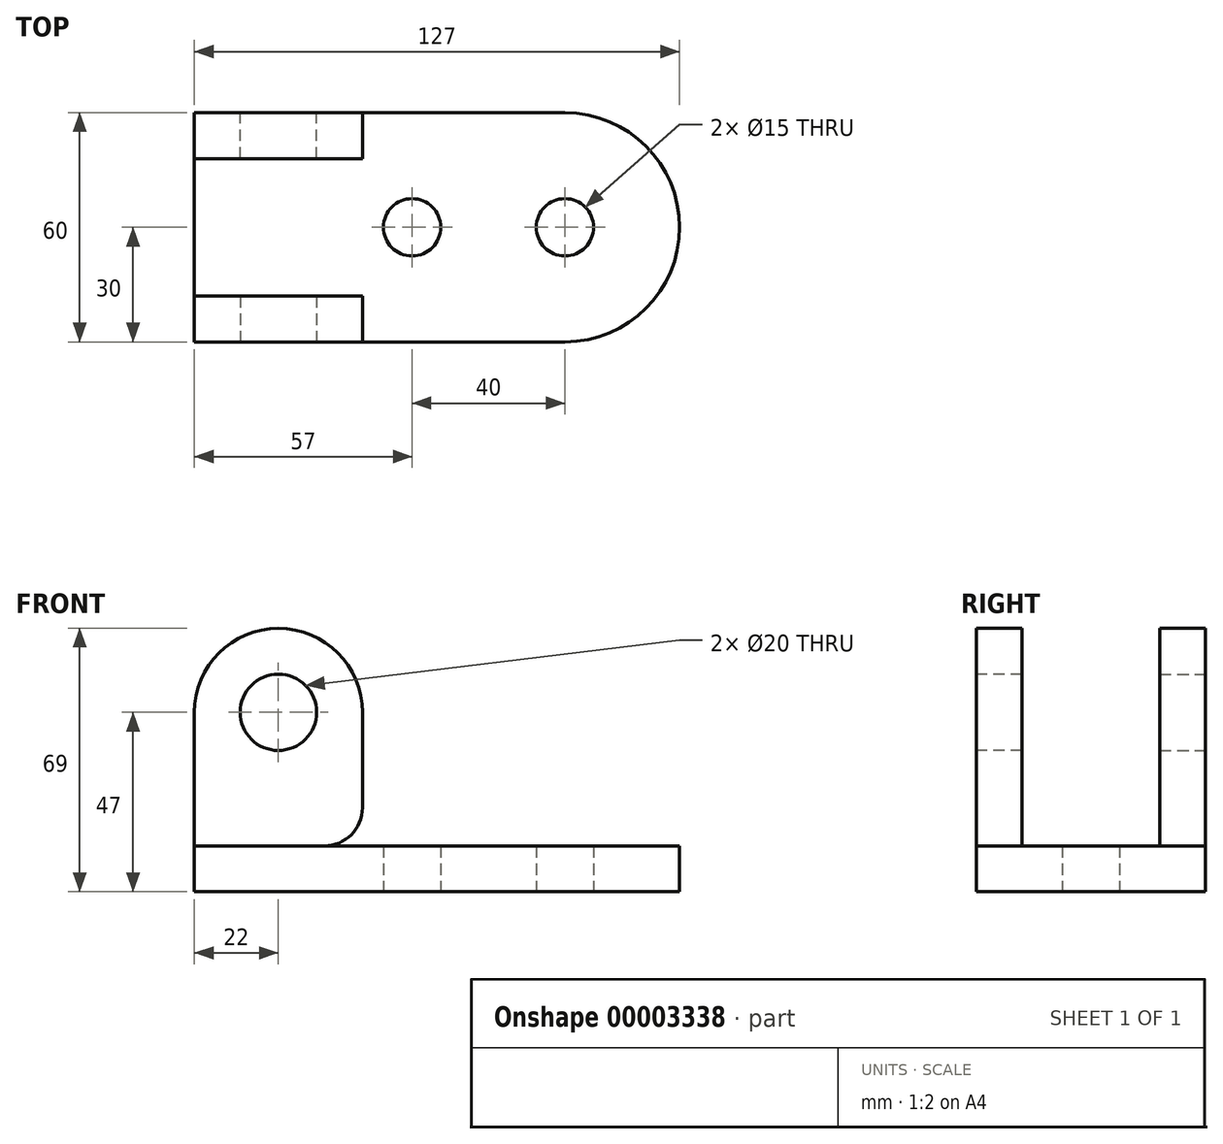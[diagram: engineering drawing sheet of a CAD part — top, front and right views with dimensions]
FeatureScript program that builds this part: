
annotation { "Feature Type Name" : "Feature", "Feature Type Description" : "" }
export const myFeature = defineFeature(function(context is Context, id is Id, definition is map)
    precondition{}
    {
        {
            var Q0;
            Q0=qCreatedBy(makeId("Top.planeOp"),FACE);
            var sketch = newSketch(context, id + "F0", { "sketchPlane" : qUnion([Q0])});
            skCircle(sketch, "E0", {"center": v(0, 0) * mm, "radius": 7.5 * mm});
            skLineSegment(sketch, "E1.bottom", {"start": v(-97, 30) * mm, "end": v(0, 30) * mm});
            skLineSegment(sketch, "E1.top", {"start": v(-97, -30) * mm, "end": v(0, -30) * mm});
            skLineSegment(sketch, "E1.left", {"start": v(-97, 30) * mm, "end": v(-97, -30) * mm});
            skLineSegment(sketch, "E1.right", {"start": v(30, 0) * mm, "end": v(30, 0) * mm});
            skPoint(sketch, "E2.visualSharp", {"position": v(30, 30) * mm});
            skArc(sketch, "E2.filletArc", {"start": v(30, 0) * mm, "mid": v(21.21, 21.21) * mm, "end": v(0, 30) * mm});
            skPoint(sketch, "E3.visualSharp", {"position": v(30, -30) * mm});
            skArc(sketch, "E3.filletArc", {"start": v(0, -30) * mm, "mid": v(21.21, -21.21) * mm, "end": v(30, 0) * mm});
            skCircle(sketch, "E4", {"center": v(-40, 0) * mm, "radius": 7.5 * mm});
            skSolve(sketch);
        }
        {
            var Q0;
            Q0=qSketchRegion(id+"F0",true);
            extrude(context, id + "F1", {"entities" : qUnion([Q0]), "depth" : 12 * mm});
        }
        {
            var Q0;
            Q0=makeQuery(id+"F1.opExtrude","SWEPT_FACE",FACE,{"disambiguationData":[OSD([sQuery(id+"F0.wireOp",EDGE,"E1.top")])]});
            var sketch = newSketch(context, id + "F2", { "sketchPlane" : qUnion([Q0])});
            skLineSegment(sketch, "E5.bottom", {"start": v(-97, 12) * mm, "end": v(-53, 12) * mm});
            skLineSegment(sketch, "E5.top", {"start": v(-75, 69) * mm, "end": v(-75, 69) * mm});
            skLineSegment(sketch, "E5.left", {"start": v(-97, 12) * mm, "end": v(-97, 47) * mm});
            skLineSegment(sketch, "E5.right", {"start": v(-53, 12) * mm, "end": v(-53, 47) * mm});
            skPoint(sketch, "E6.visualSharp", {"position": v(-97, 69) * mm});
            skArc(sketch, "E6.filletArc", {"start": v(-75, 69) * mm, "mid": v(-90.56, 62.56) * mm, "end": v(-97, 47) * mm});
            skPoint(sketch, "E7.visualSharp", {"position": v(-53, 69) * mm});
            skArc(sketch, "E7.filletArc", {"start": v(-53, 47) * mm, "mid": v(-59.44, 62.56) * mm, "end": v(-75, 69) * mm});
            skCircle(sketch, "E8", {"center": v(-75, 47) * mm, "radius": 10 * mm});
            skSolve(sketch);
        }
        {
            var Q0;
            Q0=makeQuery(id+"F2.imprint","IMPRINT",FACE,{"disambiguationData":[TD([[makeQuery(id+"F2.imprint","IMPRINT",EDGE,{"derivedFrom":sQuery(id+"F2.wireOp",EDGE,"E5.bottom")}),1.0]])]});
            extrude(context, id + "F3", {"entities" : qUnion([Q0]), "oppositeDirection" : true, "depth" : 12 * mm});
        }
        {
            var Q0;
            Q0=makeQuery(id+"F3.opExtrude","SWEPT_BODY",BODY,{"disambiguationData":[OSD([sQuery(id+"F2.wireOp",EDGE,"E5.bottom"),sQuery(id+"F2.wireOp",EDGE,"E5.left"),sQuery(id+"F2.wireOp",EDGE,"E5.right"),sQuery(id+"F2.wireOp",EDGE,"E7.filletArc"),sQuery(id+"F2.wireOp",EDGE,"E8")])]});
            var Q1;
            Q1=qCreatedBy(makeId("Front.planeOp"),FACE);
            mirror(context, id + "F4", {"entities" : qUnion([Q0]), "mirrorPlane" : qUnion([Q1])});
        }
        {
            var Q0;
            Q0=makeQuery(id+"F3.opExtrude","SWEPT_EDGE",EDGE,{"disambiguationData":[OSD([sQuery(id+"F0.wireOp",EDGE,"E1.top"),sQuery(id+"F2.wireOp",EDGE,"E5.bottom"),sQuery(id+"F2.wireOp",EDGE,"E5.right")])]});
            var Q1;
            Q1=makeQuery(id+"F4.opPattern","COPY",EDGE,{"derivedFrom":makeQuery(id+"F3.opExtrude","SWEPT_EDGE",EDGE,{"disambiguationData":[OSD([sQuery(id+"F0.wireOp",EDGE,"E1.top"),sQuery(id+"F2.wireOp",EDGE,"E5.bottom"),sQuery(id+"F2.wireOp",EDGE,"E5.right")])]}),"instanceName":"1"});
            fillet(context, id + "F5", {"entities" : qUnion([Q0, Q1]), "radius" : 10 * mm, "tangentPropagation" : true, "allowEdgeOverflow" : false});
        }
    });
